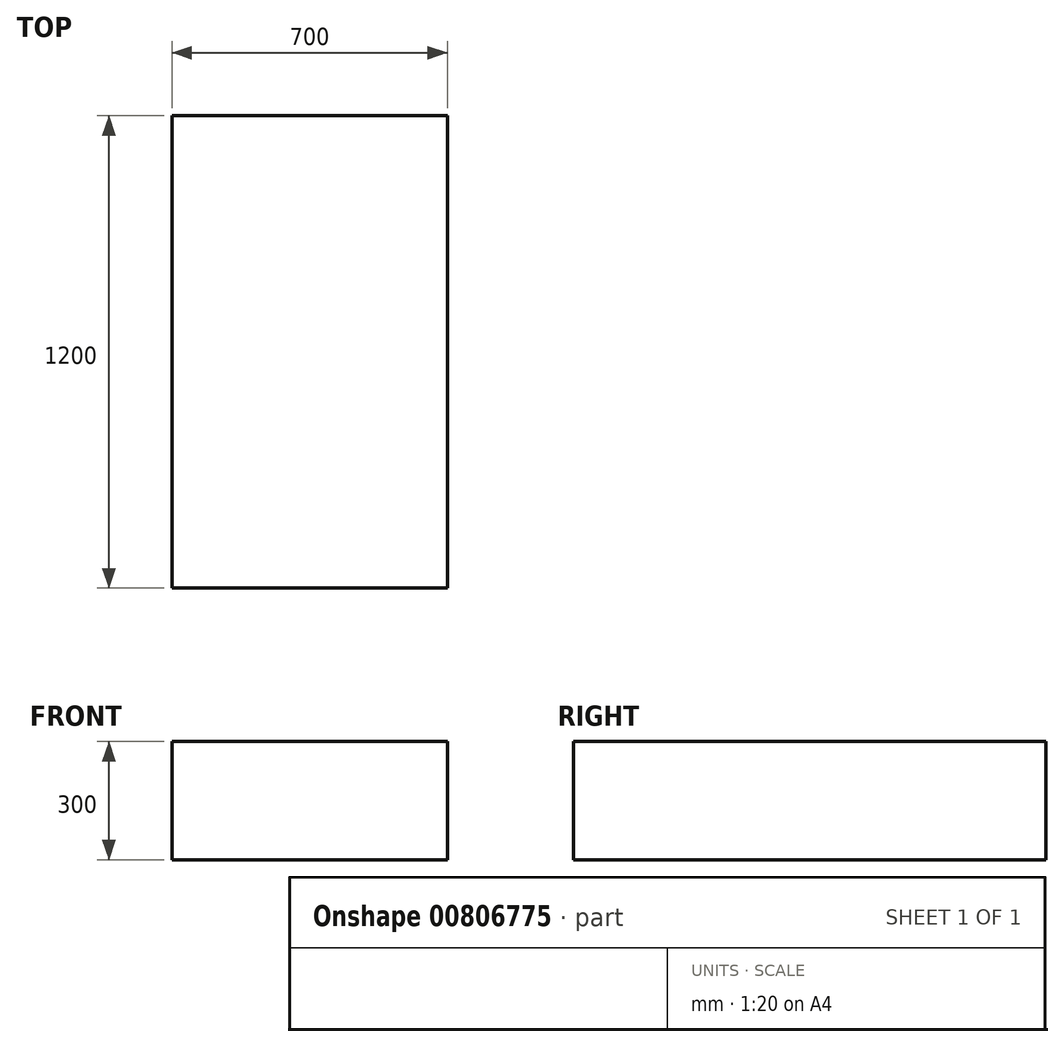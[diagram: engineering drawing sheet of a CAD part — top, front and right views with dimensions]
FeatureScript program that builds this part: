
annotation { "Feature Type Name" : "Feature", "Feature Type Description" : "" }
export const myFeature = defineFeature(function(context is Context, id is Id, definition is map)
    precondition{}
    {
        {
            var Q0;
            Q0=qCreatedBy(makeId("Front.planeOp"),FACE);
            var sketch = newSketch(context, id + "F0", { "sketchPlane" : qUnion([Q0])});
            skLineSegment(sketch, "E0.bottom", {"start": v(350, 150) * mm, "end": v(-350, 150) * mm});
            skLineSegment(sketch, "E0.top", {"start": v(350, -150) * mm, "end": v(-350, -150) * mm});
            skLineSegment(sketch, "E0.left", {"start": v(350, 150) * mm, "end": v(350, -150) * mm});
            skLineSegment(sketch, "E0.right", {"start": v(-350, 150) * mm, "end": v(-350, -150) * mm});
            skPoint(sketch, "E0.middle", {"position": v(0, 0) * mm});
            skSolve(sketch);
        }
        {
            var Q0;
            Q0=makeQuery(id+"F0.imprint","IMPRINT",FACE,{"disambiguationData":[TD([[makeQuery(id+"F0.imprint","IMPRINT",EDGE,{"derivedFrom":sQuery(id+"F0.wireOp",EDGE,"E0.bottom")}),1.0]])]});
            extrude(context, id + "F1", {"entities" : qUnion([Q0]), "depth" : 1200 * mm, "offsetDistance" : 25 * mm});
        }
    });
